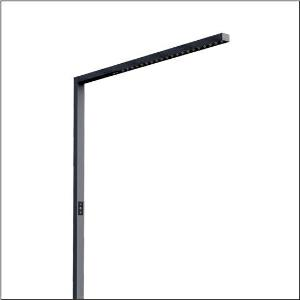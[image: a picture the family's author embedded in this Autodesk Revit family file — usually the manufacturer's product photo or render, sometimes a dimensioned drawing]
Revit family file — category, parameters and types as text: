
# Revit family: silica_r__31_floor_51my52fa3cb_e743
name_source: partatom
category: Lighting Fixtures
units: mm (PartAtom-declared; Revit-internal decimal feet)

## family parameters
Cut with Voids When Loaded = No
Host = Face
Light Source = No
Part Type = Normal
Room Calculation Point = No
Round Connector Dimension = Use Diameter
Shared = No

## types (1)
- Silica® 31 Floor (1 x LED, 10300 lm, 75 W, 3000K)
    Apparent Load = 75 VA
    CIE Flux Codes = 86 100 100 24 100
    Color Rendering = 80
    Color Temperature = 3000K
    Default Elevation = 1800 mm
    Description = Silica® 31 Floor, floorstanding luminaire, secondary optical cover: cover panel, of PMMA, light emission: direct/indirect distribution, primary light characteristic: symmetric, installation type: not mounted, LED, rated luminous flux: 10.300lm, luminous efficacy: 137lm/W, light colour: 830, colour temperature: 3000K, daylight-dependent control, with cable with plug, mains connection: 230V, AC, 50Hz, connection cable pre-assembled, rated input power: 75W, luminaire head, of aluminium, jet black (RAL 9005), length: 1.203mm, width: 52mm, supporting column, angular, of aluminium, jet black (RAL 9005), baseplate, of steel, jet black (RAL 9005), protection rating (complete): IP20, insulation class (complete): insulation class I (protective earthing), certification: CE, permissible operating ambient temperature: -20..+40°C, standard: EN 50419, packaging unit: 1 piece
    Height = 36 mm
    Lamp = 1 x LED
    Lamp Light Flux = 10300 lm
    Lamp Power = 75 W
    Lamp count = 1
    Length = 1203 mm
    Luminous efficacy = 137 lm/W
    Manufacturer = Siteco
    ModVariant = No
    Model = 51MY52FA3CB
    Mounting Place = Floor
    Mounting Type = Freestanding
    Number of Poles = 1
    OnlyDefault = Yes
    Power Factor = 1
    Product Name = Silica® 31 Floor
    Product group = floorstanding luminaire
    ProductGroupID = 1302
    Protection Class = Protection class I
    Protection Degree = IP 20
    RLX_Detail_Level = 1
    RLX_Emergency_Light_Flux = 0 lm
    RLX_Emergency_Type = 0
    RLX_Emergency_Type_DB = No
    RlxData = <blob elided: 20089 chars, md5=3abf24c1>
    Socket = socket
    Standby Power = 0 W
    System Light Flux = 10300 lm
    System Power = 75 W
    Type Comments = Product without accessories
    Type Image = l_1275297.jpg
    URL = http://relux.com
    VarID = ---
    Voltage = 0 V
    Weight = 0.00 kg
    Width = 52 mm  [stored 0.170604 ft]

note: [stored X ft] marks values corroborated as IEEE doubles in the binary element streams (Revit-internal decimal feet)

## geometry (parser evidence)
native form markers: Blend x4, Sweep x17
no freeform markers — native parametric forms only
